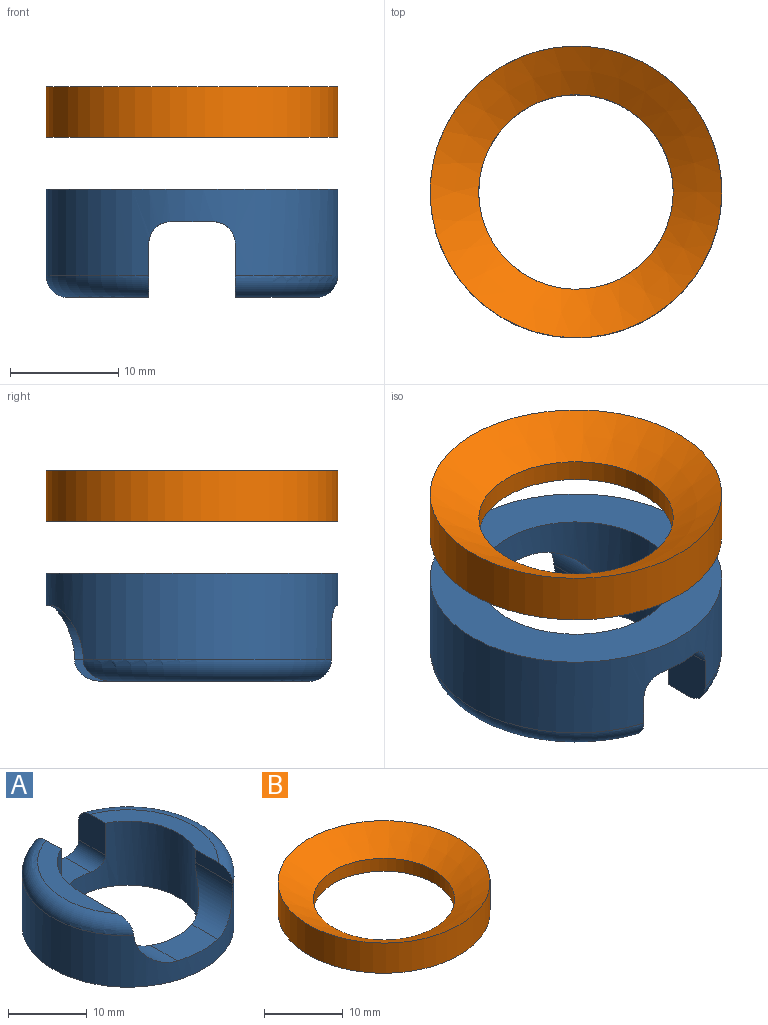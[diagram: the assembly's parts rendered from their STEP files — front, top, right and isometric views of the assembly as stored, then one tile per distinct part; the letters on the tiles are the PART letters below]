
ASSEMBLY  parts=2 mates=1
PART A: 17 faces, bbox 29.2x27.5x10 mm
  f0: plane 17.94x7.5mm, normal (0,0,1), area 42.2mm2, adj f4,f6,f8,f14
  f1: torus R=11.5mm, axis (0,0,1), area 86.1mm2, adj f2,f3,f7,f13
  f2: cylinder r=13.5mm len=27mm, axis (0,0,-1), area 560.6mm2, adj f1,f5,f6,f9,f10,f11,f12,f13
  f3: plane 19.04x7.5mm, normal (0,0,1), area 47.1mm2, adj f1,f4,f7,f13
  f4: cylinder r=9mm len=18mm, axis (0,0,-1), area 369.1mm2, adj f0,f3,f5,f7,f8,f9,f10,f11
  f5: plane 27x27mm, normal (0,0,-1), area 318.1mm2, adj f2,f4
  f6: torus R=11.5mm, axis (0,0,1), area 81.9mm2, adj f0,f2,f8,f14
  f7: plane 6.75x2mm, normal (-1,0,0), area 12.4mm2, adj f1,f3,f4,f10
  f8: plane 10.06x2mm, normal (1,0,0), area 18.9mm2, adj f0,f4,f6,f11
  f9: plane 7x5.44mm, normal (0,0,1), area 32.1mm2, adj f2,f4,f10,f11
  f10: cylinder r=5mm len=9.04mm, axis (0,1,0), area 44.7mm2, adj f2,f4,f7,f9
  f11: cylinder r=5mm len=12.89mm, axis (0,-1,0), area 52.4mm2, adj f2,f4,f8,f9
  f12: plane 4.73x4mm, normal (0,0,1), area 18.1mm2, adj f2,f4,f15,f16
  f13: plane 5x4.83mm, normal (-1,0,0), area 23.3mm2, adj f1,f2,f3,f4,f15
  f14: plane 5x4.83mm, normal (1,0,0), area 23.3mm2, adj f0,f2,f4,f6,f16
  f15: cylinder r=2mm len=5.29mm, axis (0,1,0), area 14.8mm2, adj f2,f4,f12,f13
  f16: cylinder r=2mm len=5.29mm, axis (0,-1,0), area 14.8mm2, adj f2,f4,f12,f14
PART B: 4 faces, bbox 27x27x4.7 mm
  f0: cylinder r=9mm len=18mm, axis (0,0,-1), area 113.1mm2, adj f2,f3
  f1: cylinder r=13.5mm len=27mm, axis (0,0,-1), area 398.7mm2, adj f2,f3
  f2: plane 27x27mm, normal (0,0,-1), area 318.1mm2, adj f0,f1
  f3: cone r=9mm half-angle=59deg, axis (0,0,1), area 370.9mm2, adj f0,f1
PLACE A rot(axis=(1,0,0),180deg) t=(7.02,13.22,-18.46)mm
PLACE B t=(7.02,13.22,-13.65)mm
MATE cylindrical B.f0 <-> A.f4  axis (0,0,-1) through (7.02,13.22,-12.65)mm
